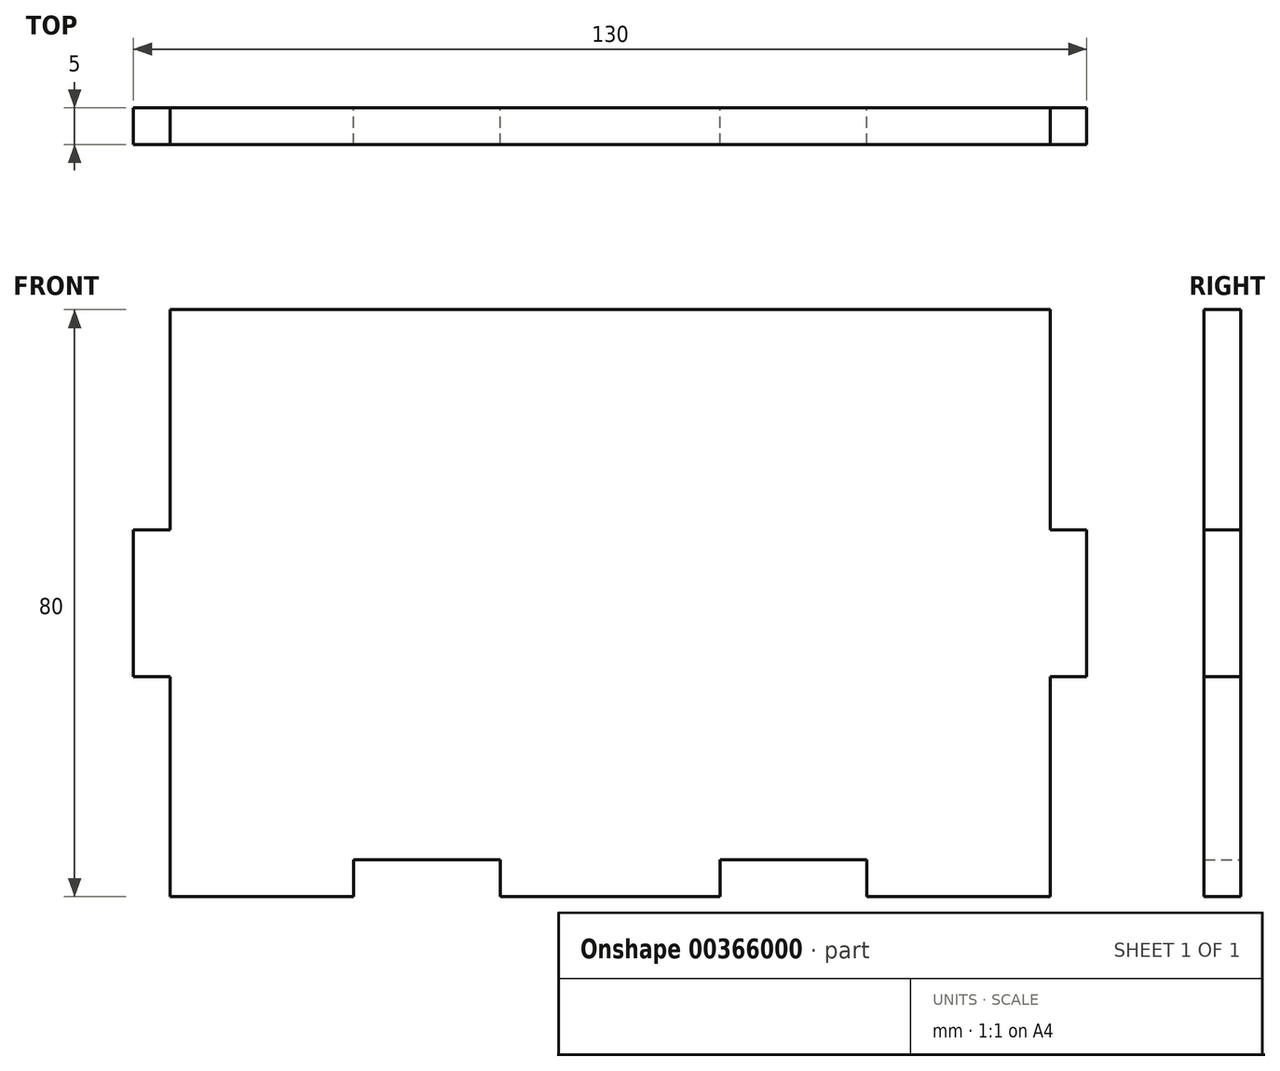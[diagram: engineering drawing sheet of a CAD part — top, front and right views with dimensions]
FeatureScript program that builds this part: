
annotation { "Feature Type Name" : "Feature", "Feature Type Description" : "" }
export const myFeature = defineFeature(function(context is Context, id is Id, definition is map)
    precondition{}
    {
        {
            var Q0;
            Q0=qCreatedBy(makeId("Front.planeOp"),FACE);
            var sketch = newSketch(context, id + "F0", { "sketchPlane" : qUnion([Q0])});
            skLineSegment(sketch, "E0", {"start": v(0, 0) * mm, "end": v(0, -30) * mm});
            skLineSegment(sketch, "E1", {"start": v(0, -30) * mm, "end": v(-5, -30) * mm});
            skLineSegment(sketch, "E2", {"start": v(-5, -30) * mm, "end": v(-5, -50) * mm});
            skLineSegment(sketch, "E3", {"start": v(-5, -50) * mm, "end": v(0, -50) * mm});
            skLineSegment(sketch, "E4", {"start": v(0, -50) * mm, "end": v(0, -80) * mm});
            skLineSegment(sketch, "E5", {"start": v(0, -80) * mm, "end": v(25, -80) * mm});
            skLineSegment(sketch, "E6", {"start": v(25, -80) * mm, "end": v(25, -75) * mm});
            skLineSegment(sketch, "E7", {"start": v(25, -75) * mm, "end": v(45, -75) * mm});
            skLineSegment(sketch, "E8", {"start": v(45, -75) * mm, "end": v(45, -80) * mm});
            skLineSegment(sketch, "E9", {"start": v(45, -80) * mm, "end": v(75, -80) * mm});
            skLineSegment(sketch, "E10", {"start": v(75, -80) * mm, "end": v(75, -75) * mm});
            skLineSegment(sketch, "E11", {"start": v(75, -75) * mm, "end": v(95, -75) * mm});
            skLineSegment(sketch, "E12", {"start": v(95, -75) * mm, "end": v(95, -80) * mm});
            skLineSegment(sketch, "E13", {"start": v(95, -80) * mm, "end": v(120, -80) * mm});
            skLineSegment(sketch, "E14", {"start": v(120, -80) * mm, "end": v(120, -50) * mm});
            skLineSegment(sketch, "E15", {"start": v(120, -50) * mm, "end": v(125, -50) * mm});
            skLineSegment(sketch, "E16", {"start": v(125, -50) * mm, "end": v(125, -30) * mm});
            skLineSegment(sketch, "E17", {"start": v(125, -30) * mm, "end": v(120, -30) * mm});
            skLineSegment(sketch, "E18", {"start": v(120, -30) * mm, "end": v(120, 0) * mm});
            skLineSegment(sketch, "E19", {"start": v(120, 0) * mm, "end": v(0, 0) * mm});
            skSolve(sketch);
        }
        {
            var Q0;
            Q0=makeQuery(id+"F0.imprint","IMPRINT",FACE,{"disambiguationData":[TD([[makeQuery(id+"F0.imprint","IMPRINT",EDGE,{"derivedFrom":sQuery(id+"F0.wireOp",EDGE,"E0")}),1.0]])]});
            extrude(context, id + "F1", {"entities" : qUnion([Q0]), "depth" : 5 * mm});
        }
    });
